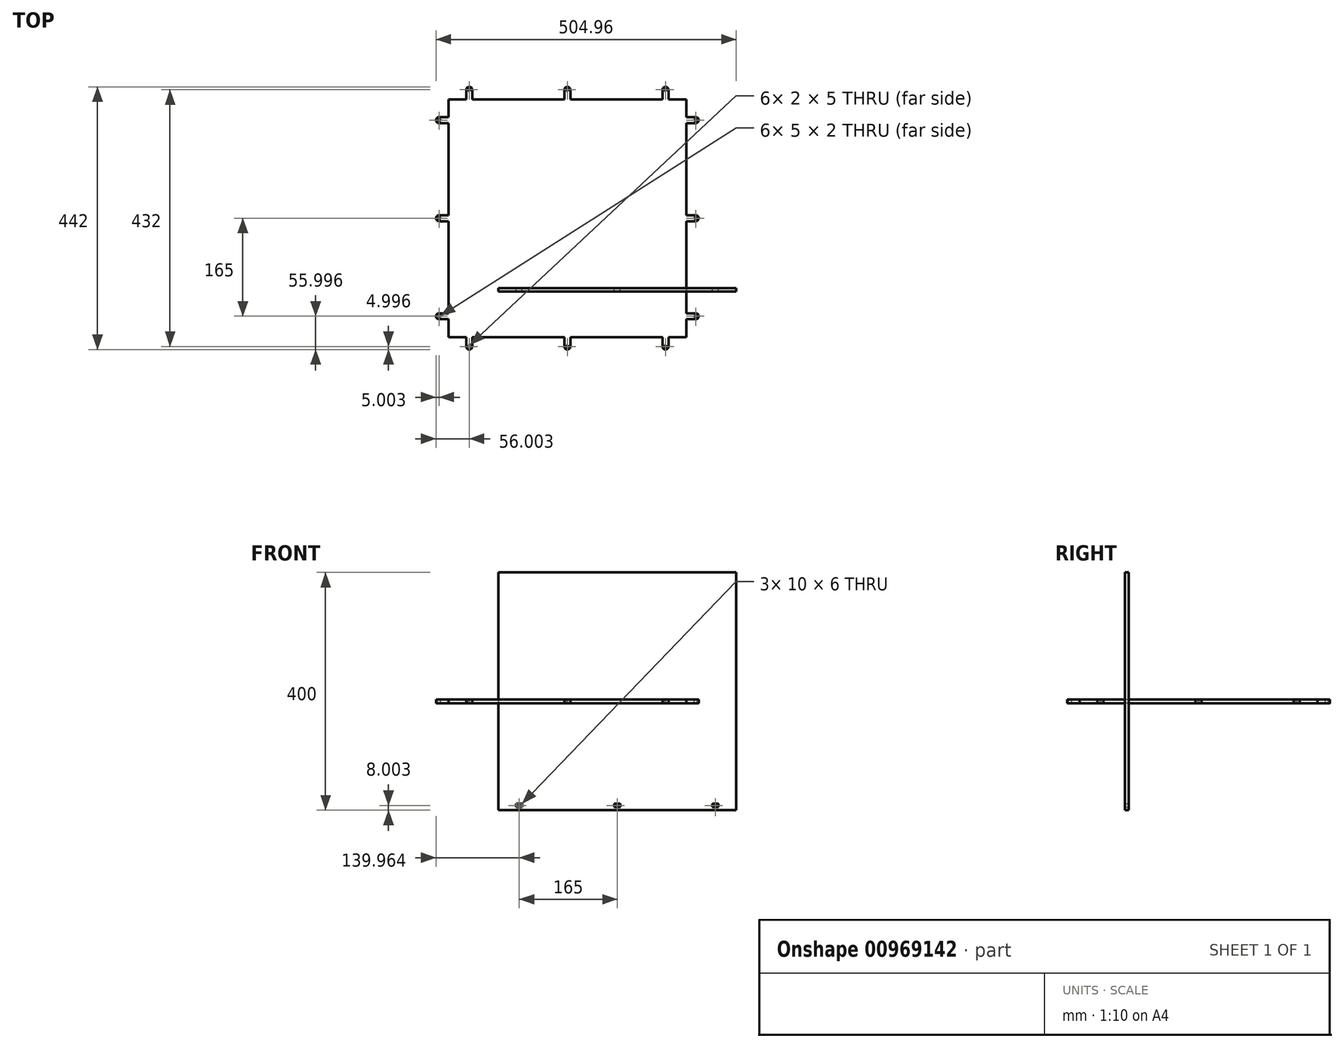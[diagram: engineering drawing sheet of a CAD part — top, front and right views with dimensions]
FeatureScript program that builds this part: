
annotation { "Feature Type Name" : "Feature", "Feature Type Description" : "" }
export const myFeature = defineFeature(function(context is Context, id is Id, definition is map)
    precondition{}
    {
        {
            var Q0;
            Q0=qCreatedBy(makeId("Top.planeOp"),FACE);
            var sketch = newSketch(context, id + "F0", { "sketchPlane" : qUnion([Q0])});
            skLineSegment(sketch, "E0.left", {"start": v(-293.85, 317.67) * mm, "end": v(-293.85, -82.33) * mm});
            skLineSegment(sketch, "E0.right", {"start": v(106.15, 317.67) * mm, "end": v(106.15, -82.33) * mm});
            skLineSegment(sketch, "E1.bottom", {"start": v(-309.85, 287.67) * mm, "end": v(-293.85, 287.67) * mm});
            skLineSegment(sketch, "E1.top", {"start": v(-309.85, 277.67) * mm, "end": v(-293.85, 277.67) * mm});
            skLineSegment(sketch, "E1.right", {"start": v(-293.85, 287.67) * mm, "end": v(-293.85, 277.67) * mm});
            skArc(sketch, "E2", {"start": v(-309.85, 287.67) * mm, "mid": v(-314.85, 282.67) * mm, "end": v(-309.85, 277.67) * mm});
            skLineSegment(sketch, "E3.bottom", {"start": v(-307.35, 281.67) * mm, "end": v(-312.35, 281.67) * mm});
            skLineSegment(sketch, "E3.top", {"start": v(-307.35, 283.67) * mm, "end": v(-312.35, 283.67) * mm});
            skLineSegment(sketch, "E3.left", {"start": v(-307.35, 281.67) * mm, "end": v(-307.35, 283.67) * mm});
            skLineSegment(sketch, "E3.right", {"start": v(-312.35, 281.67) * mm, "end": v(-312.35, 283.67) * mm});
            skLineSegment(sketch, "E4.bottom", {"start": v(-309.85, -42.33) * mm, "end": v(-293.85, -42.33) * mm});
            skLineSegment(sketch, "E4.top", {"start": v(-309.85, -52.33) * mm, "end": v(-293.85, -52.33) * mm});
            skLineSegment(sketch, "E4.right", {"start": v(-293.85, -42.33) * mm, "end": v(-293.85, -52.33) * mm});
            skArc(sketch, "E5", {"start": v(-309.85, -42.33) * mm, "mid": v(-314.85, -47.33) * mm, "end": v(-309.85, -52.33) * mm});
            skLineSegment(sketch, "E6.bottom", {"start": v(-307.35, -48.33) * mm, "end": v(-312.35, -48.33) * mm});
            skLineSegment(sketch, "E6.top", {"start": v(-307.35, -46.33) * mm, "end": v(-312.35, -46.33) * mm});
            skLineSegment(sketch, "E6.left", {"start": v(-307.35, -48.33) * mm, "end": v(-307.35, -46.33) * mm});
            skLineSegment(sketch, "E6.right", {"start": v(-312.35, -48.33) * mm, "end": v(-312.35, -46.33) * mm});
            skLineSegment(sketch, "E7.bottom", {"start": v(-309.85, 122.67) * mm, "end": v(-293.85, 122.67) * mm});
            skLineSegment(sketch, "E7.top", {"start": v(-309.85, 112.67) * mm, "end": v(-293.85, 112.67) * mm});
            skLineSegment(sketch, "E7.right", {"start": v(-293.85, 122.67) * mm, "end": v(-293.85, 112.67) * mm});
            skArc(sketch, "E8", {"start": v(-309.85, 122.67) * mm, "mid": v(-314.85, 117.67) * mm, "end": v(-309.85, 112.67) * mm});
            skLineSegment(sketch, "E9.bottom", {"start": v(-307.35, 116.67) * mm, "end": v(-312.35, 116.67) * mm});
            skLineSegment(sketch, "E9.top", {"start": v(-307.35, 118.67) * mm, "end": v(-312.35, 118.67) * mm});
            skLineSegment(sketch, "E9.left", {"start": v(-307.35, 116.67) * mm, "end": v(-307.35, 118.67) * mm});
            skLineSegment(sketch, "E9.right", {"start": v(-312.35, 116.67) * mm, "end": v(-312.35, 118.67) * mm});
            skLineSegment(sketch, "E10.bottom", {"start": v(122.15, -52.33) * mm, "end": v(106.15, -52.33) * mm});
            skLineSegment(sketch, "E10.top", {"start": v(122.15, -42.33) * mm, "end": v(106.15, -42.33) * mm});
            skLineSegment(sketch, "E10.right", {"start": v(106.15, -52.33) * mm, "end": v(106.15, -42.33) * mm});
            skArc(sketch, "E11", {"start": v(122.15, -52.33) * mm, "mid": v(127.15, -47.33) * mm, "end": v(122.15, -42.33) * mm});
            skLineSegment(sketch, "E12.bottom", {"start": v(119.65, -46.33) * mm, "end": v(124.65, -46.33) * mm});
            skLineSegment(sketch, "E12.top", {"start": v(119.65, -48.33) * mm, "end": v(124.65, -48.33) * mm});
            skLineSegment(sketch, "E12.left", {"start": v(119.65, -46.33) * mm, "end": v(119.65, -48.33) * mm});
            skLineSegment(sketch, "E12.right", {"start": v(124.65, -46.33) * mm, "end": v(124.65, -48.33) * mm});
            skLineSegment(sketch, "E13.bottom", {"start": v(122.15, 277.67) * mm, "end": v(106.15, 277.67) * mm});
            skLineSegment(sketch, "E13.top", {"start": v(122.15, 287.67) * mm, "end": v(106.15, 287.67) * mm});
            skLineSegment(sketch, "E13.right", {"start": v(106.15, 277.67) * mm, "end": v(106.15, 287.67) * mm});
            skArc(sketch, "E14", {"start": v(122.15, 277.67) * mm, "mid": v(127.15, 282.67) * mm, "end": v(122.15, 287.67) * mm});
            skLineSegment(sketch, "E15.bottom", {"start": v(119.65, 283.67) * mm, "end": v(124.65, 283.67) * mm});
            skLineSegment(sketch, "E15.top", {"start": v(119.65, 281.67) * mm, "end": v(124.65, 281.67) * mm});
            skLineSegment(sketch, "E15.left", {"start": v(119.65, 283.67) * mm, "end": v(119.65, 281.67) * mm});
            skLineSegment(sketch, "E15.right", {"start": v(124.65, 283.67) * mm, "end": v(124.65, 281.67) * mm});
            skLineSegment(sketch, "E16.bottom", {"start": v(122.15, 112.67) * mm, "end": v(106.15, 112.67) * mm});
            skLineSegment(sketch, "E16.top", {"start": v(122.15, 122.67) * mm, "end": v(106.15, 122.67) * mm});
            skLineSegment(sketch, "E16.right", {"start": v(106.15, 112.67) * mm, "end": v(106.15, 122.67) * mm});
            skArc(sketch, "E17", {"start": v(122.15, 112.67) * mm, "mid": v(127.15, 117.67) * mm, "end": v(122.15, 122.67) * mm});
            skLineSegment(sketch, "E18.bottom", {"start": v(119.65, 118.67) * mm, "end": v(124.65, 118.67) * mm});
            skLineSegment(sketch, "E18.top", {"start": v(119.65, 116.67) * mm, "end": v(124.65, 116.67) * mm});
            skLineSegment(sketch, "E18.left", {"start": v(119.65, 118.67) * mm, "end": v(119.65, 116.67) * mm});
            skLineSegment(sketch, "E18.right", {"start": v(124.65, 118.67) * mm, "end": v(124.65, 116.67) * mm});
            skLineSegment(sketch, "E19.left", {"start": v(-293.85, -82.33) * mm, "end": v(106.15, -82.33) * mm});
            skLineSegment(sketch, "E19.right", {"start": v(-293.85, 317.67) * mm, "end": v(106.15, 317.67) * mm});
            skLineSegment(sketch, "E20.bottom", {"start": v(-263.85, -98.33) * mm, "end": v(-263.85, -82.33) * mm});
            skLineSegment(sketch, "E20.top", {"start": v(-253.85, -98.33) * mm, "end": v(-253.85, -82.33) * mm});
            skLineSegment(sketch, "E20.right", {"start": v(-263.85, -82.33) * mm, "end": v(-253.85, -82.33) * mm});
            skArc(sketch, "E21", {"start": v(-263.85, -98.33) * mm, "mid": v(-258.85, -103.33) * mm, "end": v(-253.85, -98.33) * mm});
            skLineSegment(sketch, "E22.bottom", {"start": v(-257.85, -95.83) * mm, "end": v(-257.85, -100.83) * mm});
            skLineSegment(sketch, "E22.top", {"start": v(-259.85, -95.83) * mm, "end": v(-259.85, -100.83) * mm});
            skLineSegment(sketch, "E22.left", {"start": v(-257.85, -95.83) * mm, "end": v(-259.85, -95.83) * mm});
            skLineSegment(sketch, "E22.right", {"start": v(-257.85, -100.83) * mm, "end": v(-259.85, -100.83) * mm});
            skLineSegment(sketch, "E23.bottom", {"start": v(66.15, -98.33) * mm, "end": v(66.15, -82.33) * mm});
            skLineSegment(sketch, "E23.top", {"start": v(76.15, -98.33) * mm, "end": v(76.15, -82.33) * mm});
            skLineSegment(sketch, "E23.right", {"start": v(66.15, -82.33) * mm, "end": v(76.15, -82.33) * mm});
            skArc(sketch, "E24", {"start": v(66.15, -98.33) * mm, "mid": v(71.15, -103.33) * mm, "end": v(76.15, -98.33) * mm});
            skLineSegment(sketch, "E25.bottom", {"start": v(72.15, -95.83) * mm, "end": v(72.15, -100.83) * mm});
            skLineSegment(sketch, "E25.top", {"start": v(70.15, -95.83) * mm, "end": v(70.15, -100.83) * mm});
            skLineSegment(sketch, "E25.left", {"start": v(72.15, -95.83) * mm, "end": v(70.15, -95.83) * mm});
            skLineSegment(sketch, "E25.right", {"start": v(72.15, -100.83) * mm, "end": v(70.15, -100.83) * mm});
            skLineSegment(sketch, "E26.bottom", {"start": v(-98.85, -98.33) * mm, "end": v(-98.85, -82.33) * mm});
            skLineSegment(sketch, "E26.top", {"start": v(-88.85, -98.33) * mm, "end": v(-88.85, -82.33) * mm});
            skLineSegment(sketch, "E26.right", {"start": v(-98.85, -82.33) * mm, "end": v(-88.85, -82.33) * mm});
            skArc(sketch, "E27", {"start": v(-98.85, -98.33) * mm, "mid": v(-93.85, -103.33) * mm, "end": v(-88.85, -98.33) * mm});
            skLineSegment(sketch, "E28.bottom", {"start": v(-92.85, -95.83) * mm, "end": v(-92.85, -100.83) * mm});
            skLineSegment(sketch, "E28.top", {"start": v(-94.85, -95.83) * mm, "end": v(-94.85, -100.83) * mm});
            skLineSegment(sketch, "E28.left", {"start": v(-92.85, -95.83) * mm, "end": v(-94.85, -95.83) * mm});
            skLineSegment(sketch, "E28.right", {"start": v(-92.85, -100.83) * mm, "end": v(-94.85, -100.83) * mm});
            skLineSegment(sketch, "E29.bottom", {"start": v(76.15, 333.67) * mm, "end": v(76.15, 317.67) * mm});
            skLineSegment(sketch, "E29.top", {"start": v(66.15, 333.67) * mm, "end": v(66.15, 317.67) * mm});
            skLineSegment(sketch, "E29.right", {"start": v(76.15, 317.67) * mm, "end": v(66.15, 317.67) * mm});
            skArc(sketch, "E30", {"start": v(76.15, 333.67) * mm, "mid": v(71.15, 338.67) * mm, "end": v(66.15, 333.67) * mm});
            skLineSegment(sketch, "E31.bottom", {"start": v(70.15, 331.17) * mm, "end": v(70.15, 336.17) * mm});
            skLineSegment(sketch, "E31.top", {"start": v(72.15, 331.17) * mm, "end": v(72.15, 336.17) * mm});
            skLineSegment(sketch, "E31.left", {"start": v(70.15, 331.17) * mm, "end": v(72.15, 331.17) * mm});
            skLineSegment(sketch, "E31.right", {"start": v(70.15, 336.17) * mm, "end": v(72.15, 336.17) * mm});
            skLineSegment(sketch, "E32.bottom", {"start": v(-253.85, 333.67) * mm, "end": v(-253.85, 317.67) * mm});
            skLineSegment(sketch, "E32.top", {"start": v(-263.85, 333.67) * mm, "end": v(-263.85, 317.67) * mm});
            skLineSegment(sketch, "E32.right", {"start": v(-253.85, 317.67) * mm, "end": v(-263.85, 317.67) * mm});
            skArc(sketch, "E33", {"start": v(-253.85, 333.67) * mm, "mid": v(-258.85, 338.67) * mm, "end": v(-263.85, 333.67) * mm});
            skLineSegment(sketch, "E34.bottom", {"start": v(-259.85, 331.17) * mm, "end": v(-259.85, 336.17) * mm});
            skLineSegment(sketch, "E34.top", {"start": v(-257.85, 331.17) * mm, "end": v(-257.85, 336.17) * mm});
            skLineSegment(sketch, "E34.left", {"start": v(-259.85, 331.17) * mm, "end": v(-257.85, 331.17) * mm});
            skLineSegment(sketch, "E34.right", {"start": v(-259.85, 336.17) * mm, "end": v(-257.85, 336.17) * mm});
            skLineSegment(sketch, "E35.bottom", {"start": v(-88.85, 333.67) * mm, "end": v(-88.85, 317.67) * mm});
            skLineSegment(sketch, "E35.top", {"start": v(-98.85, 333.67) * mm, "end": v(-98.85, 317.67) * mm});
            skLineSegment(sketch, "E35.right", {"start": v(-88.85, 317.67) * mm, "end": v(-98.85, 317.67) * mm});
            skArc(sketch, "E36", {"start": v(-88.85, 333.67) * mm, "mid": v(-93.85, 338.67) * mm, "end": v(-98.85, 333.67) * mm});
            skLineSegment(sketch, "E37.bottom", {"start": v(-94.85, 331.17) * mm, "end": v(-94.85, 336.17) * mm});
            skLineSegment(sketch, "E37.top", {"start": v(-92.85, 331.17) * mm, "end": v(-92.85, 336.17) * mm});
            skLineSegment(sketch, "E37.left", {"start": v(-94.85, 331.17) * mm, "end": v(-92.85, 331.17) * mm});
            skLineSegment(sketch, "E37.right", {"start": v(-94.85, 336.17) * mm, "end": v(-92.85, 336.17) * mm});
            skSolve(sketch);
        }
        {
            var Q0;
            {var subQ16=sQuery(id+"F0.wireOp",EDGE,"E0.left");var subQ26=makeQuery(id+"F0.imprint","INTERSECT",VERTEX,{"derivedFrom":[subQ16,sQuery(id+"F0.wireOp",EDGE,"E1.top")]});Q0=makeQuery(id+"F0.imprint","IMPRINT",FACE,{"disambiguationData":[TD([[makeQuery(id+"F0.imprint","IMPRINT",EDGE,{"disambiguationData":[TD([[subQ26,-1.0]])],"derivedFrom":subQ16}),1.0]])]});}
            var Q1;
            {var subQ1=sQuery(id+"F0.wireOp",EDGE,"E4.bottom");Q1=makeQuery(id+"F0.imprint","IMPRINT",FACE,{"disambiguationData":[TD([[makeQuery(id+"F0.imprint","IMPRINT",EDGE,{"derivedFrom":subQ1}),-1.0]])]});}
            var Q2;
            {var subQ1=sQuery(id+"F0.wireOp",EDGE,"E7.bottom");Q2=makeQuery(id+"F0.imprint","IMPRINT",FACE,{"disambiguationData":[TD([[makeQuery(id+"F0.imprint","IMPRINT",EDGE,{"derivedFrom":subQ1}),-1.0]])]});}
            var Q3;
            {var subQ2=sQuery(id+"F0.wireOp",EDGE,"E1.bottom");Q3=makeQuery(id+"F0.imprint","IMPRINT",FACE,{"disambiguationData":[TD([[makeQuery(id+"F0.imprint","IMPRINT",EDGE,{"derivedFrom":subQ2}),-1.0]])]});}
            var Q4;
            Q4=makeQuery(id+"F0.imprint","IMPRINT",FACE,{"disambiguationData":[TD([[makeQuery(id+"F0.imprint","IMPRINT",EDGE,{"derivedFrom":sQuery(id+"F0.wireOp",EDGE,"a9a17031-c760-433b-ac6b-232ff5e79839.bottom")}),-1.0]])]});
            var Q5;
            Q5=makeQuery(id+"F0.imprint","IMPRINT",FACE,{"disambiguationData":[TD([[makeQuery(id+"F0.imprint","IMPRINT",EDGE,{"derivedFrom":sQuery(id+"F0.wireOp",EDGE,"25dab7be-3be2-42c5-bdf8-470080fdea2a.bottom")}),-1.0]])]});
            var Q6;
            Q6=makeQuery(id+"F0.imprint","IMPRINT",FACE,{"disambiguationData":[TD([[makeQuery(id+"F0.imprint","IMPRINT",EDGE,{"derivedFrom":sQuery(id+"F0.wireOp",EDGE,"71e0ab8f-6807-4fe2-b55d-4a4277cce7f2.bottom")}),-1.0]])]});
            var Q7;
            {var subQ1=sQuery(id+"F0.wireOp",EDGE,"E10.bottom");Q7=makeQuery(id+"F0.imprint","IMPRINT",FACE,{"disambiguationData":[TD([[makeQuery(id+"F0.imprint","IMPRINT",EDGE,{"derivedFrom":subQ1}),-1.0]])]});}
            var Q8;
            {var subQ1=sQuery(id+"F0.wireOp",EDGE,"E16.bottom");Q8=makeQuery(id+"F0.imprint","IMPRINT",FACE,{"disambiguationData":[TD([[makeQuery(id+"F0.imprint","IMPRINT",EDGE,{"derivedFrom":subQ1}),-1.0]])]});}
            var Q9;
            {var subQ0=sQuery(id+"F0.wireOp",EDGE,"E13.bottom");Q9=makeQuery(id+"F0.imprint","IMPRINT",FACE,{"disambiguationData":[TD([[makeQuery(id+"F0.imprint","IMPRINT",EDGE,{"derivedFrom":subQ0}),-1.0]])]});}
            var Q10;
            Q10=makeQuery(id+"F0.imprint","IMPRINT",FACE,{"disambiguationData":[TD([[makeQuery(id+"F0.imprint","IMPRINT",EDGE,{"derivedFrom":sQuery(id+"F0.wireOp",EDGE,"e0994c86-e813-4f8a-901d-c0888817f6ac.bottom")}),-1.0]])]});
            var Q11;
            Q11=makeQuery(id+"F0.imprint","IMPRINT",FACE,{"disambiguationData":[TD([[makeQuery(id+"F0.imprint","IMPRINT",EDGE,{"derivedFrom":sQuery(id+"F0.wireOp",EDGE,"1959c640-5de6-41dd-a2b4-4dba6dd70c89.bottom")}),-1.0]])]});
            var Q12;
            Q12=makeQuery(id+"F0.imprint","IMPRINT",FACE,{"disambiguationData":[TD([[makeQuery(id+"F0.imprint","IMPRINT",EDGE,{"derivedFrom":sQuery(id+"F0.wireOp",EDGE,"45a3ede4-fb5b-4ec1-9970-23c1b8f26049.bottom")}),-1.0]])]});
            var Q13;
            {var subQ2=sQuery(id+"F0.wireOp",EDGE,"E20.bottom");Q13=makeQuery(id+"F0.imprint","IMPRINT",FACE,{"disambiguationData":[TD([[makeQuery(id+"F0.imprint","IMPRINT",EDGE,{"derivedFrom":subQ2}),-1.0]])]});}
            var Q14;
            {var subQ1=sQuery(id+"F0.wireOp",EDGE,"E26.bottom");Q14=makeQuery(id+"F0.imprint","IMPRINT",FACE,{"disambiguationData":[TD([[makeQuery(id+"F0.imprint","IMPRINT",EDGE,{"derivedFrom":subQ1}),-1.0]])]});}
            var Q15;
            {var subQ1=sQuery(id+"F0.wireOp",EDGE,"E23.bottom");Q15=makeQuery(id+"F0.imprint","IMPRINT",FACE,{"disambiguationData":[TD([[makeQuery(id+"F0.imprint","IMPRINT",EDGE,{"derivedFrom":subQ1}),-1.0]])]});}
            var Q16;
            {var subQ1=sQuery(id+"F0.wireOp",EDGE,"E29.bottom");Q16=makeQuery(id+"F0.imprint","IMPRINT",FACE,{"disambiguationData":[TD([[makeQuery(id+"F0.imprint","IMPRINT",EDGE,{"derivedFrom":subQ1}),-1.0]])]});}
            var Q17;
            {var subQ1=sQuery(id+"F0.wireOp",EDGE,"E35.bottom");Q17=makeQuery(id+"F0.imprint","IMPRINT",FACE,{"disambiguationData":[TD([[makeQuery(id+"F0.imprint","IMPRINT",EDGE,{"derivedFrom":subQ1}),-1.0]])]});}
            var Q18;
            {var subQ0=sQuery(id+"F0.wireOp",EDGE,"E32.bottom");Q18=makeQuery(id+"F0.imprint","IMPRINT",FACE,{"disambiguationData":[TD([[makeQuery(id+"F0.imprint","IMPRINT",EDGE,{"derivedFrom":subQ0}),-1.0]])]});}
            extrude(context, id + "F1", {"entities" : qUnion([Q0, Q1, Q2, Q3, Q4, Q5, Q6, Q7, Q8, Q9, Q10, Q11, Q12, Q13, Q14, Q15, Q16, Q17, Q18]), "oppositeDirection" : true, "depth" : 6.1 * mm, "offsetDistance" : 25 * mm});
        }
        {
            var Q0;
            Q0=qCreatedBy(makeId("Front.planeOp"),FACE);
            var sketch = newSketch(context, id + "F2", { "sketchPlane" : qUnion([Q0])});
            skLineSegment(sketch, "E38.bottom", {"start": v(-209.89, 213.96) * mm, "end": v(190.11, 213.96) * mm});
            skLineSegment(sketch, "E38.top", {"start": v(-209.89, -186.04) * mm, "end": v(190.11, -186.04) * mm});
            skLineSegment(sketch, "E38.left", {"start": v(-209.89, 213.96) * mm, "end": v(-209.89, -186.04) * mm});
            skLineSegment(sketch, "E38.right", {"start": v(190.11, 213.96) * mm, "end": v(190.11, -186.04) * mm});
            skLineSegment(sketch, "E39.bottom", {"start": v(-179.89, -175.04) * mm, "end": v(-169.89, -175.04) * mm});
            skLineSegment(sketch, "E39.top", {"start": v(-179.89, -181.04) * mm, "end": v(-169.89, -181.04) * mm});
            skLineSegment(sketch, "E39.left", {"start": v(-179.89, -175.04) * mm, "end": v(-179.89, -181.04) * mm});
            skLineSegment(sketch, "E39.right", {"start": v(-169.89, -175.04) * mm, "end": v(-169.89, -181.04) * mm});
            skLineSegment(sketch, "E40.bottom", {"start": v(150.11, -175.04) * mm, "end": v(160.11, -175.04) * mm});
            skLineSegment(sketch, "E40.top", {"start": v(150.11, -181.04) * mm, "end": v(160.11, -181.04) * mm});
            skLineSegment(sketch, "E40.left", {"start": v(150.11, -175.04) * mm, "end": v(150.11, -181.04) * mm});
            skLineSegment(sketch, "E40.right", {"start": v(160.11, -175.04) * mm, "end": v(160.11, -181.04) * mm});
            skLineSegment(sketch, "E41.bottom", {"start": v(-14.89, -175.04) * mm, "end": v(-4.89, -175.04) * mm});
            skLineSegment(sketch, "E41.top", {"start": v(-14.89, -181.04) * mm, "end": v(-4.89, -181.04) * mm});
            skLineSegment(sketch, "E41.left", {"start": v(-14.89, -175.04) * mm, "end": v(-14.89, -181.04) * mm});
            skLineSegment(sketch, "E41.right", {"start": v(-4.89, -175.04) * mm, "end": v(-4.89, -181.04) * mm});
            skSolve(sketch);
        }
        {
            var Q0;
            Q0=makeQuery(id+"F2.imprint","IMPRINT",FACE,{"disambiguationData":[TD([[makeQuery(id+"F2.imprint","IMPRINT",EDGE,{"derivedFrom":sQuery(id+"F2.wireOp",EDGE,"E38.bottom")}),-1.0]])]});
            extrude(context, id + "F3", {"entities" : qUnion([Q0]), "depth" : 6 * mm, "offsetDistance" : 25 * mm});
        }
    });
